# Revit family: Sink_Double_Bowl_Drop-In-Elkay-DRKAD371765RC
name_source: partatom
category: Plumbing Fixtures
units: mm (PartAtom-declared; Revit-internal decimal feet)

## family parameters
Cut with Voids When Loaded = No
Host = Face
Maintain Annotation Orientation = No
OmniClass Number = 23.45.05.14.14
OmniClass Title = Sinks/Lavatories
Part Type = Normal
Room Calculation Point = No
Round Connector Dimension = Use Diameter
Shared = No

## types (1)
- DRKAD371765RC (Double Bowl Drop-In Classroom Sink)
    Approx. Shipping Weight (lbs) = 27
    Assembly Code = D2010.60
    Bowl 1 Dimensions = 16 inch x 11 1/2 inch x 6 3/8 inch
    Bowl 2 Dimensions = 9 1/4 inch x 12 inch x 3 1/2 inch
    CW Connection = Yes
    Default Elevation = 48.000"
    Description = Lustertone® Classic Stainless Steel 37 1/4 inch x 17 inch x 6 1/2 inch Double Bowl Drop-in Classroom ADA Sink
    Drain Location = Center
    Drain Size = 3 1/2 inch, 2 inch
    HW Connection = Yes
    Inlet Connection Size (inch) = 0.500"
    Installation Type = Drop-In
    Main Material = Finish-Elkay-Stainless Steel
    Manufacturer = Elkay Manufacturer Company
    Manufacturer Brand = Elkay (by Zurn Elkay Water Solutions)
    Model = DRKAD371765RC
    No of Bowls = 2
    Outlet Connection Size (inch) = 1.500"
    Product Documentation Link = https://www.elkayfiles.com
    Product Installation Sheet URL = https://www.elkayfiles.com
    Product Page URL = https://www.elkay.com
    Product Weight (lbs) = 22
    Product data URL = https://www.bimobject.com
    Repair Parts URL = https://www.elkayfiles.com
    Sink Dimensions = 37 1/4 inch x 17 inch x 6 1/2 inch
    URL = https://www.elkay.com
    Vent Connection = No
    Waste Connection = Yes

## geometry (parser evidence)
native form markers: Sweep x16
no freeform markers — native parametric forms only
